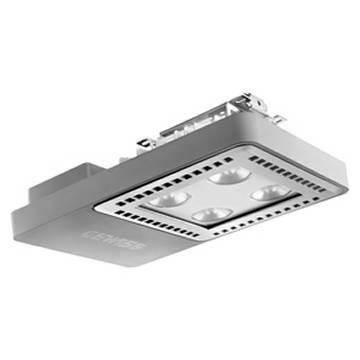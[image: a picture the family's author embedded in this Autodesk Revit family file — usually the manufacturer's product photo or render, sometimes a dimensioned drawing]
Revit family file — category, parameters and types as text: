
# Revit family: Lighting-Industrial-GEWISS-SMART[4]HLO_HIGHBAYS-LED_1M
name_source: partatom
category: Apparecchi per illuminazione
units: mm (PartAtom-declared; Revit-internal decimal feet)

## family parameters
Basato su piano di lavoro = Sì
Condiviso = No
Numero OmniClass = 23.80.00.00
Punto di calcolo locali = No
Quota connettore circolare = Usa diametro
Sempre verticale = No
Sorgente d'illuminazione = No
Taglio con vuoti quando caricato = No
Tipo di parte = Normale
Titolo OmniClass = Electric Power and Lighting

## types (36) — shared parameters
Application = Internal
Body = PA6 "Halogen Free" loaded fibreglass
Carico apparente = 50 VA
Catalogue = LIGHTING
Classification: = -
Classificazione = Lighting
Color Rendering Index = CRI-80
Colour = Grey RAL 7035
Colour : = Grey RAL 7035
Commenti sul wattaggio = 50W
Context = Logistics and industrial manufacturing lighting
Control System = ON / OFF
Control System : = ON / OFF
DIN 18032-3 certification = With Bracket - Rope Kit + terminal&nbsp;(in approval)
Device with reduced surface temperature = Yes
Distanza tot_plafoniera = 74 mm  [stored 0.242782 ft]
Driver = Included
Driver Box = Built-in
Electrocod = 2444
Eletrical and lighting features = -
External screw = Stainless steel
Fixing = -
Gasket = anti-aging silicone
General information = -
Glow Wire Test : = 850 °C
IDF = 4926170b-ab71-4dd4-9d69-00cd3560e388
IDT = 38a7e34fee1a4d0d9e54b5fc2166bea5
IP degree = IP66
IPEA = -
Immagine tipo = GWL1071.jpg
Installationa and maintenance = -
Insulation class = I
LED Maintenance = Non-replaceable
Lampada = LED
Larghezza = 253 mm  [stored 0.830052 ft]
Lifetime = L90B10 (Tq+25°C) = 70.000 h - L90B10 (Tq+50°C) = 35.000 h
Locking Hook = -
Luminaire = LED Industrial ReflectorÂ
Lunghezza = 383 mm  [stored 1.25656 ft]
Materials = -
Maximum surface exposed to the wind : = 0,097 m²
Motore = <Per categoria>
Mouting and installation = Ceiling - Wallmounting - Suspension
Operating temperature : = -30°C ÷ +50 °C
Optic Maintenance = Non-replaceable
Optic and illuminating features = -
Overvoltage protection = DM 6kV / CM 6kV
Photobiological Risk Class = RG0
Plafoniera = <Per categoria>
Produttore = GEWISS S.p.A.
Prospetto di default = 1219 mm
Raggio led = 30 mm  [stored 0.0984252 ft]
Rated frequency (Hz) = 50/60 Hz
Shield type = Tempered glass Thickness 4mm
Shock resistance = IK08
Spessore plafoniera = 40 mm  [stored 0.131234 ft]
Standard Deviation Colour Matching = SDCM = 3
Standard- = EN 60598-1 ; EN 60598-2-1 ; EN 60598-2-24
Standards and approvals = -
Stocking temperature = -40 +70 °C
Supply voltage = 220 - 240 V
System power = 64W
Technical sheet = https://www.gewiss.com
Tilt- = With bracket accessory
Trasformatore = <Per categoria>
Type of light source = LED - Not replaceable
URL = https://www.gewiss.com
Unique digital code (Datamatrix) = Datamatrix
Version file RFA = 20.11
Vetro acceso = Lampada accesa
Voltaggio = 230 V
Warranty = 5 years
Weight (kg): = 3,5
Wiring = With GW connect watertight connector

## per-type parameters (varying)
| type | Colour temperature | Descrizione | Efficiency (lm/W) | Lumen output (lm) | Modello | Optic | Optic : | SEO | Unified Glare Rating |
| GWS4122BA857 - SMART4LB 1M C.PAS.ON/OFF HLO ARR.57K | 5700K | SMART[4]LB 1M C.PAS.ON/OFF HLO ARR.57K | 144 | 9200 | GWS4122BA857 | Array | Metallized polycarbonate reflector |  | - |
| GWS4122BC857 - SMART4LB 1M C.PAS.ON/OFF HLO ASI.57K | 5700K | SMART[4]LB 1M C.PAS.ON/OFF HLO ASI.57K | 128 | 8200 | GWS4122BC857 | Asymmetrical | Metallic PC reflector and PMMA lenses | Low bay | - |
| GWS4122BF840 - SMART4LB 1M C.PAS.ON/OFF HLO 30° 40K | 4000K | SMART[4]LB 1M C.PAS.ON/OFF HLO 30° 40K | 141 | 9000 | GWS4122BF840 | 30° | Metallic PC reflector and PMMA lenses |  | UGR - 22 |
| GWS4120BQ857 - SMART4LB 1M ST.AL.ON/OFF HLO ELL.57K | 5700K | SMART[4]LB 1M ST.AL.ON/OFF HLO ELL.57K | 128 | 8200 | GWS4120BQ857 | Elliptical | Metallic PC reflector and PMMA lenses | Low bay | - |
| GWS4120BC830 - SMART4LB 1M ST.AL.ON/OFF HLO ASI.30K | 3000K | SMART[4]LB 1M ST.AL.ON/OFF HLO ASI.30K | 122 | 7800 | GWS4120BC830 | Asymmetrical | Metallic PC reflector and PMMA lenses | Low bay | - |
| GWS4122BC830 - SMART4LB 1M C.PAS.ON/OFF HLO ASI.30K | 3000K | SMART[4]LB 1M C.PAS.ON/OFF HLO ASI.30K | 122 | 7800 | GWS4122BC830 | Asymmetrical | Metallic PC reflector and PMMA lenses | Low bay | - |
| GWS4120BH857 - SMART4LB 1M ST.AL.ON/OFF HLO 60° 57K | 5700K | SMART[4]LB 1M ST.AL.ON/OFF HLO 60° 57K | 144 | 9200 | GWS4120BH857 | 60° | Metallic PC reflector and PMMA lenses |  | UGR - 25 |
| GWS4120BA857 - SMART4LB 1M ST.AL.ON/OFF HLO ARR.57K | 5700K | SMART[4]LB 1M ST.AL.ON/OFF HLO ARR.57K | 144 | 9200 | GWS4120BA857 | Array | Metallized polycarbonate reflector |  | - |
| GWS4120BP840 - SMART4LB 1M ST.AL.ON/OFF HLO 90° 40K | 4000K | SMART[4]LB 1M ST.AL.ON/OFF HLO 90° 40K | 144 | 9200 | GWS4120BP840 | 90° | Metallic PC reflector and PMMA lenses |  | UGR - 25 |
| GWS4122BQ830 - SMART4LB 1M C.PAS.ON/OFF HLO ELL.30K | 3000K | SMART[4]LB 1M C.PAS.ON/OFF HLO ELL.30K | 122 | 7800 | GWS4122BQ830 | Elliptical | Metallic PC reflector and PMMA lenses | Low bay | - |
| GWS4120BC840 - SMART4LB 1M ST.AL.ON/OFF HLO ASI.40K | 4000K | SMART[4]LB 1M ST.AL.ON/OFF HLO ASI.40K | 128 | 8200 | GWS4120BC840 | Asymmetrical | Metallic PC reflector and PMMA lenses | Low bay | - |
| GWS4122BC840 - SMART4LB 1M C.PAS.ON/OFF HLO ASI.40K | 4000K | SMART[4]LB 1M C.PAS.ON/OFF HLO ASI.40K | 128 | 8200 | GWS4122BC840 | Asymmetrical | Metallic PC reflector and PMMA lenses | Low bay | - |
| GWS4122BF830 - SMART4LB 1M C.PAS.ON/OFF HLO 30° 30K | 3000K | SMART[4]LB 1M C.PAS.ON/OFF HLO 30° 30K | 134 | 8600 | GWS4122BF830 | 30° | Metallic PC reflector and PMMA lenses |  | UGR - 22 |
| GWS4120BA830 - SMART4LB 1M ST.AL.ON/OFF HLO ARR.30K | 3000K | SMART[4]LB 1M ST.AL.ON/OFF HLO ARR.30K | 136 | 8700 | GWS4120BA830 | Array | Metallized polycarbonate reflector |  | - |
| GWS4120BP830 - SMART4LB 1M ST.AL.ON/OFF HLO 90° 30K | 3000K | SMART[4]LB 1M ST.AL.ON/OFF HLO 90° 30K | 138 | 8800 | GWS4120BP830 | 90° | Metallic PC reflector and PMMA lenses |  | UGR - 25 |
| GWS4120BF840 - SMART4LB 1M ST.AL.ON/OFF HLO 30° 40K | 4000K | SMART[4]LB 1M ST.AL.ON/OFF HLO 30° 40K | 141 | 9000 | GWS4120BF840 | 30° | Metallic PC reflector and PMMA lenses |  | UGR - 22 |
| GWS4120BP857 - SMART4LB 1M ST.AL.ON/OFF HLO 90° 57K | 5700K | SMART[4]LB 1M ST.AL.ON/OFF HLO 90° 57K | 144 | 9200 | GWS4120BP857 | 90° | Metallic PC reflector and PMMA lenses |  | UGR - 25 |
| GWS4122BQ840 - SMART4LB 1M C.PAS.ON/OFF HLO ELL.40K | 4000K | SMART[4]LB 1M C.PAS.ON/OFF HLO ELL.40K | 128 | 8200 | GWS4122BQ840 | Elliptical | Metallic PC reflector and PMMA lenses | Low bay | - |
| GWS4120BQ840 - SMART4LB 1M ST.AL.ON/OFF HLO ELL.40K | 4000K | SMART[4]LB 1M ST.AL.ON/OFF HLO ELL.40K | 128 | 8200 | GWS4120BQ840 | Elliptical | Metallic PC reflector and PMMA lenses | Low bay | - |
| GWS4120BH840 - SMART4LB 1M ST.AL.ON/OFF HLO 60° 40K | 4000K | SMART[4]LB 1M ST.AL.ON/OFF HLO 60° 40K | 144 | 9200 | GWS4120BH840 | 60° | Metallic PC reflector and PMMA lenses |  | UGR - 25 |
| GWS4120BA840 - SMART4LB 1M ST.AL.ON/OFF HLO ARR.40K | 4000K | SMART[4]LB 1M ST.AL.ON/OFF HLO ARR.40K | 144 | 9200 | GWS4120BA840 | Array | Metallized polycarbonate reflector |  | - |
| GWS4122BH857 - SMART4LB 1M C.PAS.ON/OFF HLO 60° 57K | 5700K | SMART[4]LB 1M C.PAS.ON/OFF HLO 60° 57K | 144 | 9200 | GWS4122BH857 | 60° | Metallic PC reflector and PMMA lenses |  | UGR - 25 |
| GWS4122BF857 - SMART4LB 1M C.PAS.ON/OFF HLO 30° 57K | 5700K | SMART[4]LB 1M C.PAS.ON/OFF HLO 30° 57K | 141 | 9000 | GWS4122BF857 | 30° | Metallic PC reflector and PMMA lenses |  | UGR - 22 |
| GWS4122BP830 - SMART4LB 1M C.PAS.ON/OFF HLO 90° 30K | 3000K | SMART[4]LB 1M C.PAS.ON/OFF HLO 90° 30K | 138 | 8800 | GWS4122BP830 | 90° | Metallic PC reflector and PMMA lenses |  | UGR - 25 |
| GWS4122BH830 - SMART4LB 1M C.PAS.ON/OFF HLO 60° 30K | 3000K | SMART[4]LB 1M C.PAS.ON/OFF HLO 60° 30K | 136 | 8700 | GWS4122BH830 | 60° | Metallic PC reflector and PMMA lenses |  | UGR - 25 |
| GWS4120BF857 - SMART4LB 1M ST.AL.ON/OFF HLO 30° 57K | 5700K | SMART[4]LB 1M ST.AL.ON/OFF HLO 30° 57K | 141 | 9000 | GWS4120BF857 | 30° | Metallic PC reflector and PMMA lenses |  | UGR - 22 |
| GWS4122BP857 - SMART4LB 1M C.PAS.ON/OFF HLO 90° 57K | 5700K | SMART[4]LB 1M C.PAS.ON/OFF HLO 90° 57K | 144 | 9200 | GWS4122BP857 | 90° | Metallic PC reflector and PMMA lenses |  | UGR - 25 |
| GWS4120BQ830 - SMART4LB 1M ST.AL.ON/OFF HLO ELL.30K | 3000K | SMART[4]LB 1M ST.AL.ON/OFF HLO ELL.30K | 122 | 7800 | GWS4120BQ830 | Elliptical | Metallic PC reflector and PMMA lenses | Low bay | - |
| GWS4122BP840 - SMART4LB 1M C.PAS.ON/OFF HLO 90° 40K | 4000K | SMART[4]LB 1M C.PAS.ON/OFF HLO 90° 40K | 144 | 9200 | GWS4122BP840 | 90° | Metallic PC reflector and PMMA lenses |  | UGR - 25 |
| GWS4120BC857 - SMART4LB 1M ST.AL.ON/OFF HLO ASI.57K | 5700K | SMART[4]LB 1M ST.AL.ON/OFF HLO ASI.57K | 128 | 8200 | GWS4120BC857 | Asymmetrical | Metallic PC reflector and PMMA lenses | Low bay | - |
| GWS4122BA840 - SMART4LB 1M C.PAS.ON/OFF HLO ARR.40K | 4000K | SMART[4]LB 1M C.PAS.ON/OFF HLO ARR.40K | 144 | 9200 | GWS4122BA840 | Array | Metallized polycarbonate reflector |  | - |
| GWS4120BF830 - SMART4LB 1M ST.AL.ON/OFF HLO 30° 30K | 3000K | SMART[4]LB 1M ST.AL.ON/OFF HLO 30° 30K | 134 | 8600 | GWS4120BF830 | 30° | Metallic PC reflector and PMMA lenses |  | UGR - 22 |
| GWS4122BH840 - SMART4LB 1M C.PAS.ON/OFF HLO 60° 40K | 4000K | SMART[4]LB 1M C.PAS.ON/OFF HLO 60° 40K | 144 | 9200 | GWS4122BH840 | 60° | Metallic PC reflector and PMMA lenses |  | UGR - 25 |
| GWS4122BA830 - SMART4LB 1M C.PAS.ON/OFF HLO ARR.30K | 3000K | SMART[4]LB 1M C.PAS.ON/OFF HLO ARR.30K | 136 | 8700 | GWS4122BA830 | Array | Metallized polycarbonate reflector |  | - |
| GWS4122BQ857 - SMART4LB 1M C.PAS.ON/OFF HLO ELL.57K | 5700K | SMART[4]LB 1M C.PAS.ON/OFF HLO ELL.57K | 128 | 8200 | GWS4122BQ857 | Elliptical | Metallic PC reflector and PMMA lenses | Low bay | - |
| GWS4120BH830 - SMART4LB 1M ST.AL.ON/OFF HLO 60° 30K | 3000K | SMART[4]LB 1M ST.AL.ON/OFF HLO 60° 30K | 136 | 8700 | GWS4120BH830 | 60° | Metallic PC reflector and PMMA lenses |  | UGR - 25 |

note: [stored X ft] marks values corroborated as IEEE doubles in the binary element streams (Revit-internal decimal feet)

## geometry (parser evidence)
native form markers: Blend x4
no freeform markers — native parametric forms only
